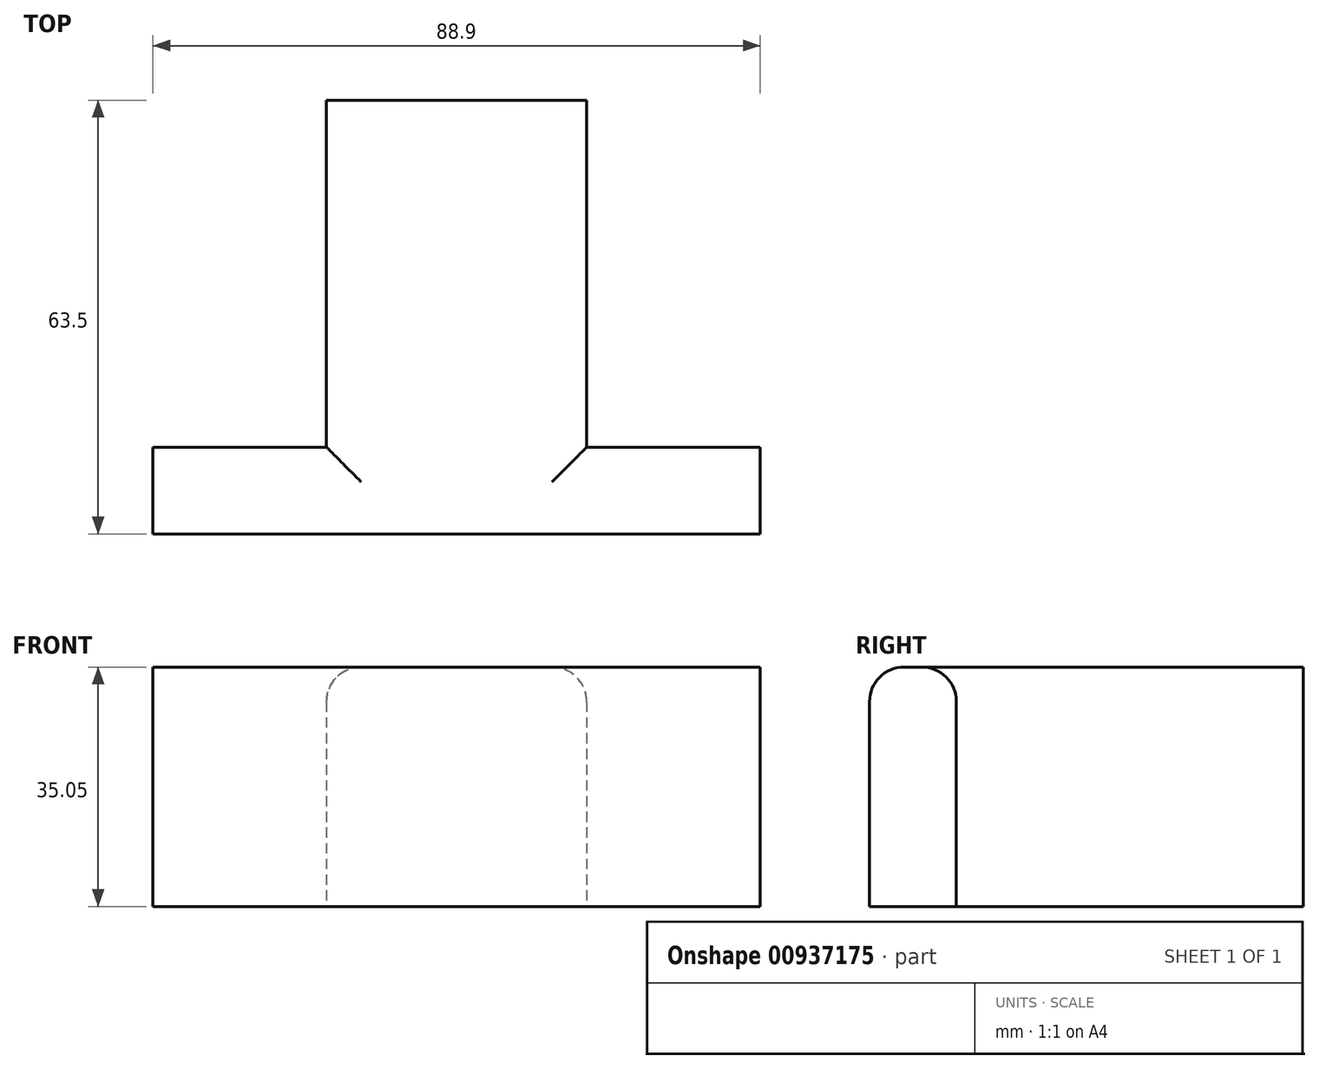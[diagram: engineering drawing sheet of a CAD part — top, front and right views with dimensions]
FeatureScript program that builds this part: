
annotation { "Feature Type Name" : "Feature", "Feature Type Description" : "" }
export const myFeature = defineFeature(function(context is Context, id is Id, definition is map)
    precondition{}
    {
        {
            var Q0;
            Q0=qCreatedBy(makeId("Top.planeOp"),FACE);
            var sketch = newSketch(context, id + "F0", { "sketchPlane" : qUnion([Q0])});
            skLineSegment(sketch, "E0.bottom", {"start": v(-13.84, 39.96) * mm, "end": v(24.26, 39.96) * mm});
            skLineSegment(sketch, "E0.top", {"start": v(-13.84, -10.84) * mm, "end": v(24.26, -10.84) * mm});
            skLineSegment(sketch, "E0.left", {"start": v(-13.84, 39.96) * mm, "end": v(-13.84, -10.84) * mm});
            skLineSegment(sketch, "E0.right", {"start": v(24.26, 39.96) * mm, "end": v(24.26, -10.84) * mm});
            skLineSegment(sketch, "E1.bottom", {"start": v(24.26, -10.84) * mm, "end": v(49.66, -10.84) * mm});
            skLineSegment(sketch, "E1.top", {"start": v(24.26, -23.54) * mm, "end": v(49.66, -23.54) * mm});
            skLineSegment(sketch, "E1.left", {"start": v(24.26, -10.84) * mm, "end": v(24.26, -23.54) * mm});
            skLineSegment(sketch, "E1.right", {"start": v(49.66, -10.84) * mm, "end": v(49.66, -23.54) * mm});
            skLineSegment(sketch, "E2.bottom", {"start": v(-13.84, -10.84) * mm, "end": v(-39.24, -10.84) * mm});
            skLineSegment(sketch, "E2.top", {"start": v(-13.84, -23.54) * mm, "end": v(-39.24, -23.54) * mm});
            skLineSegment(sketch, "E2.left", {"start": v(-13.84, -10.84) * mm, "end": v(-13.84, -23.54) * mm});
            skLineSegment(sketch, "E2.right", {"start": v(-39.24, -10.84) * mm, "end": v(-39.24, -23.54) * mm});
            skLineSegment(sketch, "E3.bottom", {"start": v(-13.84, -23.54) * mm, "end": v(24.26, -23.54) * mm});
            skLineSegment(sketch, "E3.left", {"start": v(-13.84, -23.54) * mm, "end": v(-13.84, -10.84) * mm});
            skLineSegment(sketch, "E3.right", {"start": v(24.26, -23.54) * mm, "end": v(24.26, -10.84) * mm});
            skSolve(sketch);
        }
        {
            var Q0;
            Q0 = qSketchRegion(id + "F0", true);
            var Q1;
            Q1=makeQuery(id+"F0.imprint","IMPRINT",FACE,{"disambiguationData":[TD([[makeQuery(id+"F0.imprint","IMPRINT",EDGE,{"derivedFrom":sQuery(id+"F0.wireOp",EDGE,"E0.bottom")}),-1.0]])]});
            extrude(context, id + "F1", {"entities" : qUnion([Q0, Q1]), "depth" : 35.05 * mm, "offsetDistance" : 25.4 * mm});
        }
        {
            var Q0;
            Q0=makeQuery(id+"F1.opExtrude","CAP_EDGE",EDGE,{"disambiguationData":[OSD([sQuery(id+"F0.wireOp",EDGE,"E0.right")])],"isStart":false});
            var Q1;
            Q1=makeQuery(id+"F1.opExtrude","CAP_EDGE",EDGE,{"disambiguationData":[OSD([sQuery(id+"F0.wireOp",EDGE,"E0.left")])],"isStart":false});
            var Q2;
            Q2=makeQuery(id+"F1.opExtrude","CAP_EDGE",EDGE,{"disambiguationData":[OSD([sQuery(id+"F0.wireOp",EDGE,"E2.bottom")])],"isStart":false});
            var Q3;
            Q3=makeQuery(id+"F1.opExtrude","CAP_EDGE",EDGE,{"disambiguationData":[OSD([sQuery(id+"F0.wireOp",EDGE,"E1.bottom")])],"isStart":false});
            var Q4;
            Q4=makeQuery(id+"F1.opExtrude","CAP_EDGE",EDGE,{"disambiguationData":[OSD([sQuery(id+"F0.wireOp",EDGE,"E1.top"),sQuery(id+"F0.wireOp",EDGE,"E2.top"),sQuery(id+"F0.wireOp",EDGE,"E3.bottom")])],"isStart":false});
            fillet(context, id + "F2", {"entities" : qUnion([Q0, Q1, Q2, Q3, Q4]), "radius" : 5.08 * mm, "tangentPropagation" : true, "allowEdgeOverflow" : false});
        }
    });
